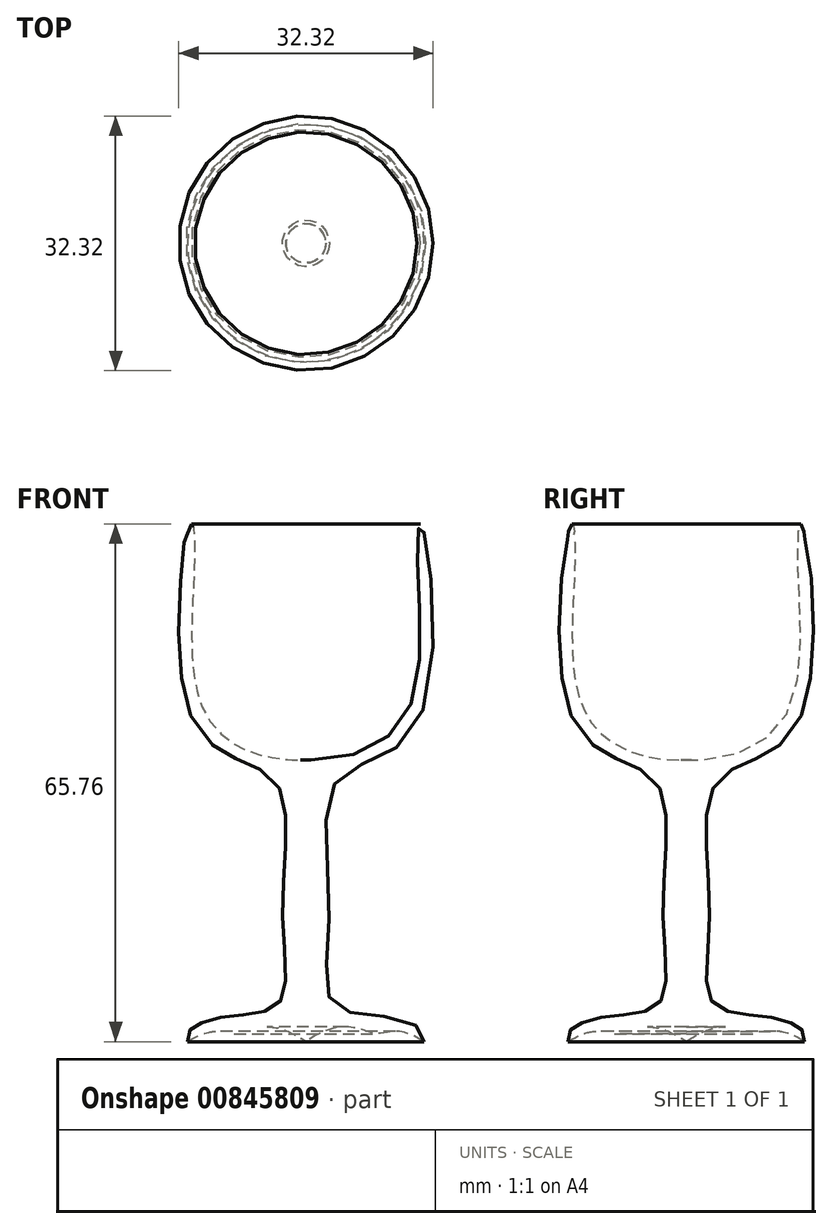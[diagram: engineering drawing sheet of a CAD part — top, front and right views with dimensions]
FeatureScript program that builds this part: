
annotation { "Feature Type Name" : "Feature", "Feature Type Description" : "" }
export const myFeature = defineFeature(function(context is Context, id is Id, definition is map)
    precondition{}
    {
        {
            var Q0;
            Q0=qCreatedBy(makeId("Front.planeOp"),FACE);
            var sketch = newSketch(context, id + "F0", { "sketchPlane" : qUnion([Q0])});
            skFitSpline(sketch, "E0", {"points": [v(0, 0) * mm, v(15.02, 0) * mm, v(12.44, 2.73) * mm, v(3.64, 4.66) * mm, v(2.97, 16.4) * mm, v(3.97, 33.17) * mm, v(14.15, 40.4) * mm, v(14.66, 65.66) * mm, v(14.15, 61.32) * mm, v(13.03, 42.22) * mm, v(2.07, 35.82) * mm, v(-8.2, 34.78) * mm, v(-1.73, 15.6) * mm, v(0, 0) * mm]});
            skLineSegment(sketch, "E1", {"start": v(0, 70.61) * mm, "end": v(0, -26.58) * mm});
            skFitSpline(sketch, "E2", {"points": [v(15.02, 0) * mm, v(8.9, 1.03) * mm, v(0, 0) * mm], "startDerivative": vector(-23.5, 14.8) * mm, "endDerivative": vector(-26.56, -18.8) * mm});
            skSolve(sketch);
        }
        {
            var Q0;
            {var subQ0=sQuery(id+"F0.wireOp",EDGE,"E2");Q0=makeQuery(id+"F0.imprint","IMPRINT",FACE,{"disambiguationData":[TD([[makeQuery(id+"F0.imprint","IMPRINT",EDGE,{"derivedFrom":subQ0}),-1.0]])]});}
            var Q1;
            Q1=sQuery(id+"F0.wireOp",EDGE,"E1");
            revolve(context, id + "F1", {"surfaceOperationType" : NewSurfaceOperationType.NEW, "entities" : qUnion([Q0]), "axis" : qUnion([Q1]), "revolveType" : RevolveType.FULL});
        }
    });
